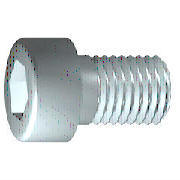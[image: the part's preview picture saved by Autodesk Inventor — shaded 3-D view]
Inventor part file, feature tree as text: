
AUTODESK INVENTOR PART (.ipt)
format: ipt  version: 2022 (Build 260153000, 153)  size: 192,000 bytes
history: native  units: mm (DEFAULTED — no unit token found)
features: sketch x2, other x1, extrude x1, plane x1, fillet x1
ambient origin geometry x7: Origin, YZ Plane, XY Plane, X Axis, Y Axis, Z Axis, Center Point
bodies: Solid1 (feature_tree)
feature tree (6):
  other  "Cuerpo"
  extrude  "Ranura"  Depth=4.0mm
  plane  "Work Plane1"
  fillet  "Fillet2"  Radius=4.0mm
  sketch  "Boceto1"  dims[d1=18.25mm d2=0.429515mm d3=4.0mm]
  sketch  "Boceto2"  dims[d4=2.0mm d5=60.0deg d6=4.0mm d7=4.0mm d8=3.464102mm d9=7.0mm d10=90.0deg d11=10.0mm d12=0.0mm d13=18.25mm d14=0.0mm d15=0.429415mm d16=0.429415mm d17=0.4mm d19=0.0mm d26=20.0mm d27=45.0deg d28=0.0mm d29=0.0mm d30=0.1mm]
